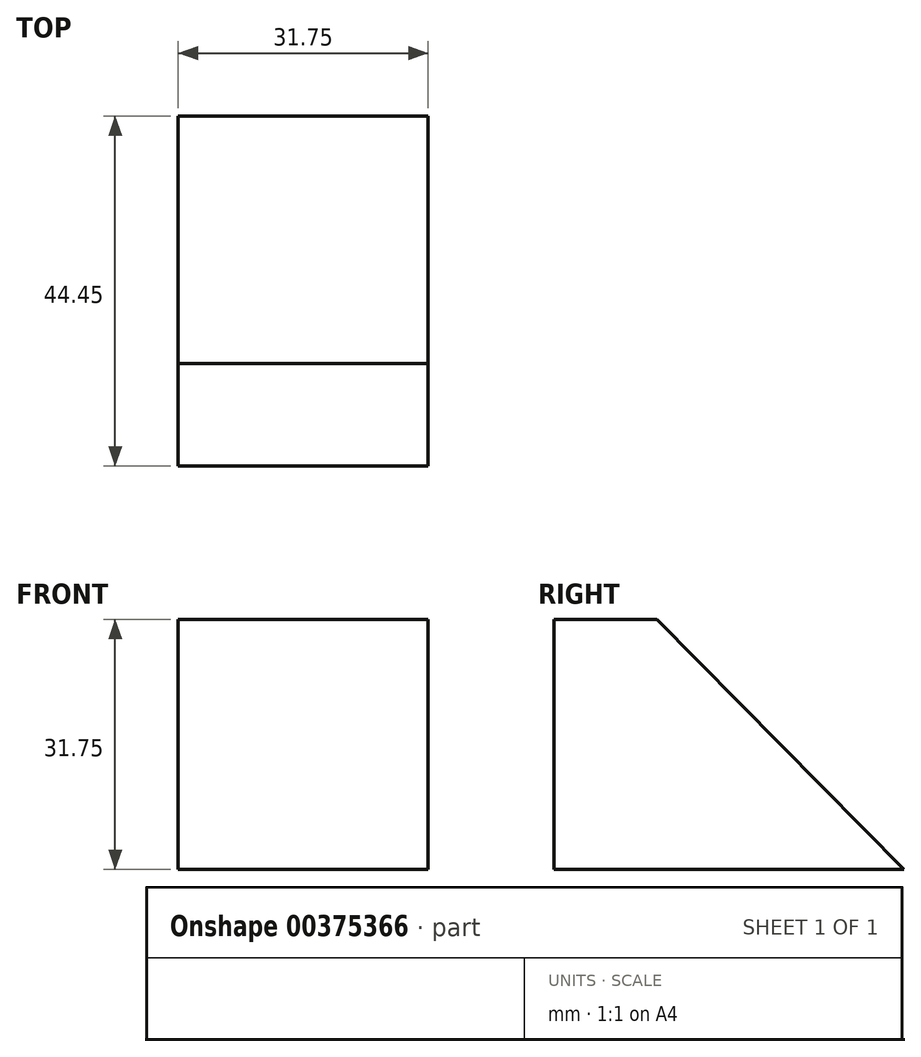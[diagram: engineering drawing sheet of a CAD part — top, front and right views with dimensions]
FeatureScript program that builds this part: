
annotation { "Feature Type Name" : "Feature", "Feature Type Description" : "" }
export const myFeature = defineFeature(function(context is Context, id is Id, definition is map)
    precondition{}
    {
        {
            var Q0;
            Q0=qCreatedBy(makeId("Right.planeOp"),FACE);
            var sketch = newSketch(context, id + "F0", { "sketchPlane" : qUnion([Q0])});
            skLineSegment(sketch, "E0", {"start": v(0, 0) * mm, "end": v(-13.04, 0) * mm});
            skLineSegment(sketch, "E1", {"start": v(-13.04, 0) * mm, "end": v(-13.04, -31.75) * mm});
            skLineSegment(sketch, "E2", {"start": v(-13.04, -31.75) * mm, "end": v(31.4, -31.75) * mm});
            skLineSegment(sketch, "E3", {"start": v(0, 0) * mm, "end": v(31.4, -31.75) * mm});
            skSolve(sketch);
        }
        {
            var Q0;
            Q0 = qSketchRegion(id + "F0", true);
            extrude(context, id + "F1", {"entities" : qUnion([Q0]), "depth" : 31.75 * mm});
        }
    });
